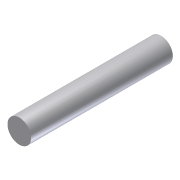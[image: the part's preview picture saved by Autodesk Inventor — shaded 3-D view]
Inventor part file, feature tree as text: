
AUTODESK INVENTOR PART (.ipt)
format: ipt  version: 2012 (Build 160160000, 160)  size: 65,024 bytes
history: native  units: in
note: dims shown in document units (in); Inventor stores cm internally (conversion verified against a paired STEP export)
features: extrude x1, sketch x1
ambient origin geometry x8: Origin, YZ Plane, XZ Plane, XY Plane, X Axis, Y Axis, Z Axis, Center Point
bodies: Solid1 (feature_tree)
feature tree (2):
  extrude  "Extrusion1"  Depth=3.0in TaperAngle=0.0deg
  sketch  "Sketch1"  dims[d0=0.5in d1=3.0in d2=0.0in]
